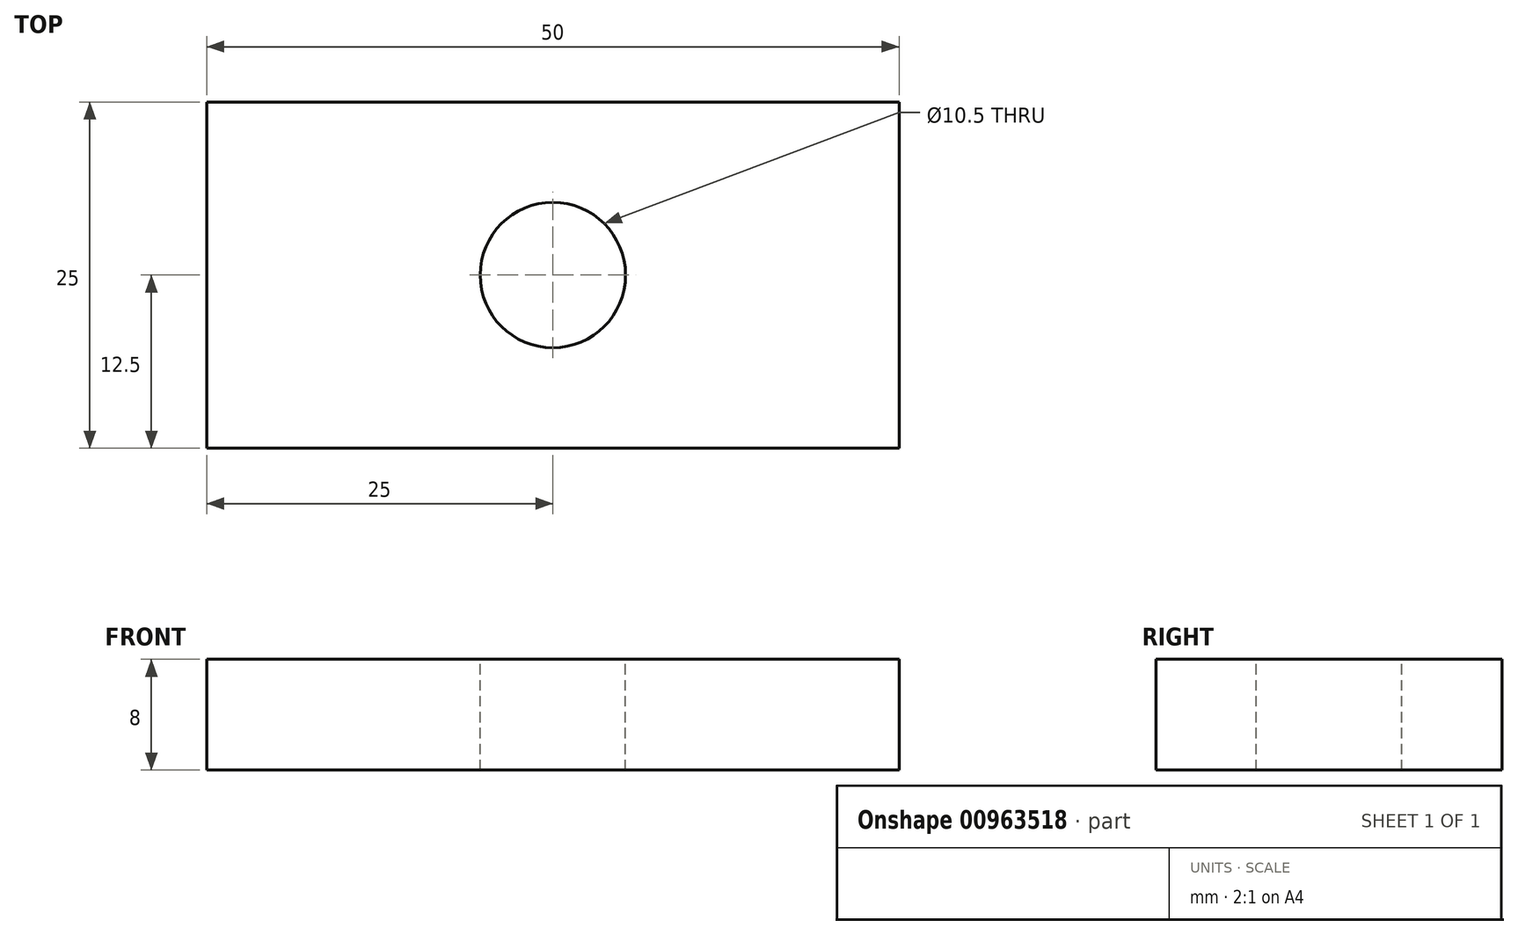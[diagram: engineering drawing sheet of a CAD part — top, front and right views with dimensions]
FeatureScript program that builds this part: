
annotation { "Feature Type Name" : "Feature", "Feature Type Description" : "" }
export const myFeature = defineFeature(function(context is Context, id is Id, definition is map)
    precondition{}
    {
        {
            var Q0;
            Q0=qCreatedBy(makeId("Top.planeOp"),FACE);
            var sketch = newSketch(context, id + "F0", { "sketchPlane" : qUnion([Q0])});
            skLineSegment(sketch, "E0.bottom", {"start": v(25, -12.5) * mm, "end": v(-25, -12.5) * mm});
            skLineSegment(sketch, "E0.top", {"start": v(25, 12.5) * mm, "end": v(-25, 12.5) * mm});
            skLineSegment(sketch, "E0.left", {"start": v(25, -12.5) * mm, "end": v(25, 12.5) * mm});
            skLineSegment(sketch, "E0.right", {"start": v(-25, -12.5) * mm, "end": v(-25, 12.5) * mm});
            skPoint(sketch, "E0.middle", {"position": v(0, 0) * mm});
            skSolve(sketch);
        }
        {
            var Q0;
            Q0=makeQuery(id+"F0.imprint","IMPRINT",FACE,{"disambiguationData":[TD([[makeQuery(id+"F0.imprint","IMPRINT",EDGE,{"derivedFrom":sQuery(id+"F0.wireOp",EDGE,"E0.bottom")}),-1.0]])]});
            extrude(context, id + "F1", {"entities" : qUnion([Q0]), "oppositeDirection" : true, "depth" : 8 * mm, "offsetDistance" : 25 * mm});
        }
        {
            var Q0;
            Q0=makeQuery(id+"F1.opExtrude","CAP_FACE",FACE,{"disambiguationData":[OSD([sQuery(id+"F0.wireOp",EDGE,"E0.bottom"),sQuery(id+"F0.wireOp",EDGE,"E0.top"),sQuery(id+"F0.wireOp",EDGE,"E0.left"),sQuery(id+"F0.wireOp",EDGE,"E0.right")])],"isStart":true});
            var sketch = newSketch(context, id + "F2", { "sketchPlane" : qUnion([Q0])});
            skCircle(sketch, "E1", {"center": v(0, 0) * mm, "radius": 5.25 * mm});
            skSolve(sketch);
        }
        {
            var Q0;
            Q0=qSketchRegion(id+"F2",true);
            extrude(context, id + "F3", {"entities" : qUnion([Q0]), "operationType" : NewBodyOperationType.REMOVE, "endBound" : BoundingType.THROUGH_ALL, "oppositeDirection" : true, "depth" : 8 * mm, "offsetDistance" : 25 * mm});
        }
    });
